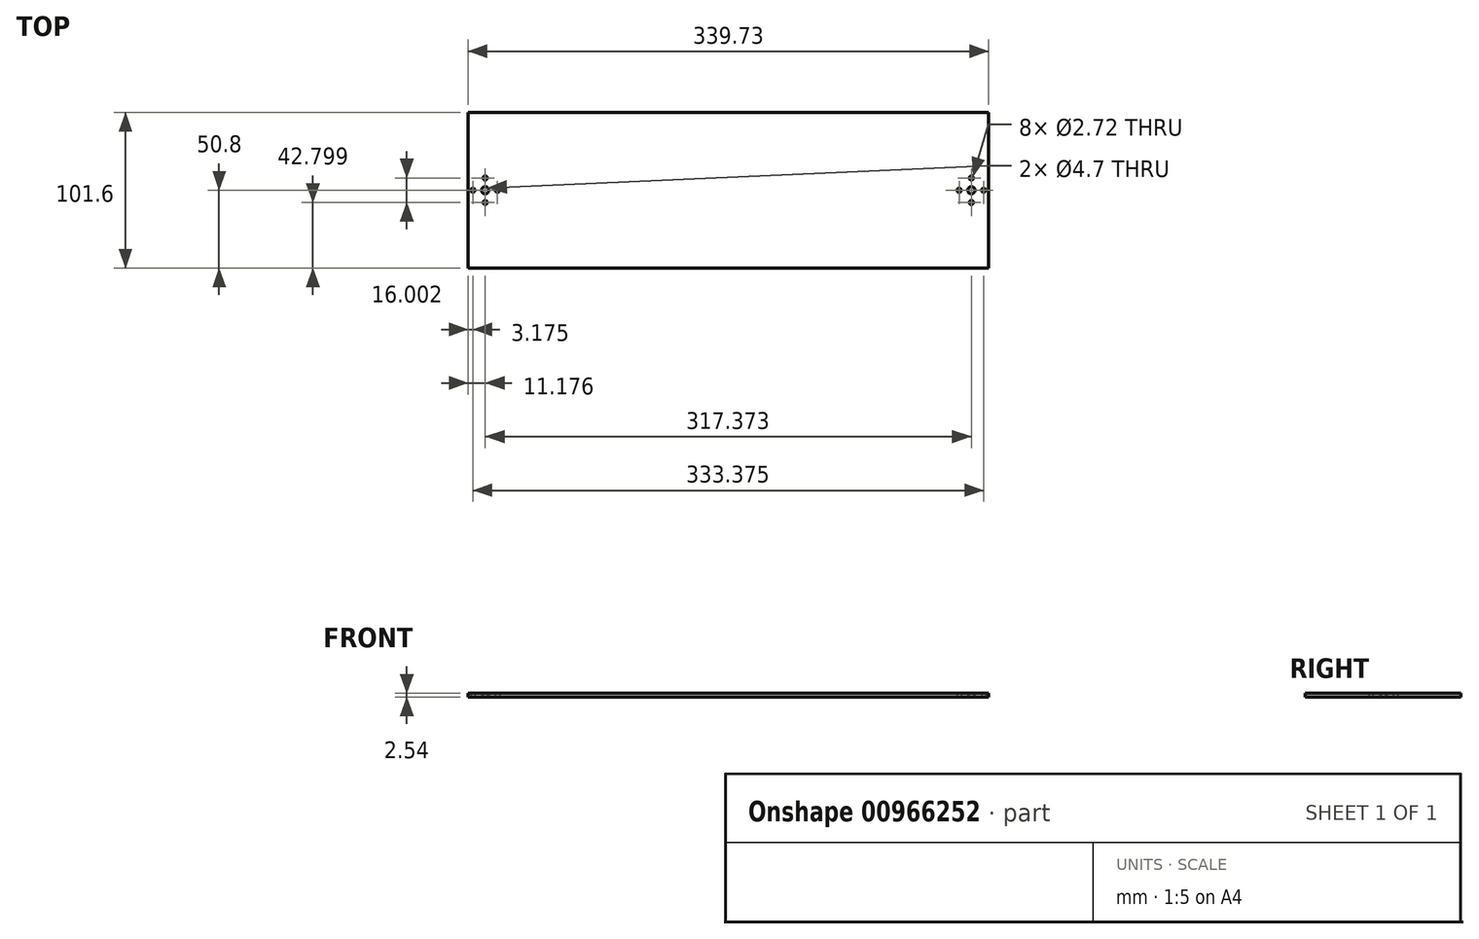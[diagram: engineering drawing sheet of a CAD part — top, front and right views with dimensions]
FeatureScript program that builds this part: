
annotation { "Feature Type Name" : "Feature", "Feature Type Description" : "" }
export const myFeature = defineFeature(function(context is Context, id is Id, definition is map)
    precondition{}
    {
        {
            var Q0;
            Q0=qCreatedBy(makeId("Top.planeOp"),FACE);
            var sketch = newSketch(context, id + "F0", { "sketchPlane" : qUnion([Q0])});
            skLineSegment(sketch, "E0.bottom", {"start": v(0, 0) * mm, "end": v(339.73, 0) * mm});
            skLineSegment(sketch, "E0.top", {"start": v(0, -101.6) * mm, "end": v(339.73, -101.6) * mm});
            skLineSegment(sketch, "E0.left", {"start": v(0, 0) * mm, "end": v(0, -101.6) * mm});
            skLineSegment(sketch, "E0.right", {"start": v(339.73, 0) * mm, "end": v(339.73, -101.6) * mm});
            skCircle(sketch, "E1", {"center": v(3.17, -50.8) * mm, "radius": 1.36 * mm});
            skPoint(sketch, "E1.centerSnap0", {"position": v(0, -50.8) * mm});
            skCircle(sketch, "E2", {"center": v(19.18, -50.8) * mm, "radius": 1.36 * mm});
            skCircle(sketch, "E3", {"center": v(11.18, -42.8) * mm, "radius": 1.36 * mm});
            skCircle(sketch, "E4", {"center": v(11.18, -58.8) * mm, "radius": 1.36 * mm});
            skCircle(sketch, "E5", {"center": v(11.18, -50.8) * mm, "radius": 2.35 * mm});
            skLineSegment(sketch, "E6", {"start": v(169.86, -101.6) * mm, "end": v(169.86, 0) * mm});
            skPoint(sketch, "E7.MirrorP", {"position": v(339.73, -50.8) * mm});
            skCircle(sketch, "E8.MirrorC", {"center": v(336.55, -50.8) * mm, "radius": 1.36 * mm});
            skCircle(sketch, "E9.MirrorC", {"center": v(320.55, -50.8) * mm, "radius": 1.36 * mm});
            skCircle(sketch, "E10.MirrorC", {"center": v(328.55, -50.8) * mm, "radius": 2.35 * mm});
            skCircle(sketch, "E11.MirrorC", {"center": v(328.55, -58.8) * mm, "radius": 1.36 * mm});
            skCircle(sketch, "E12.MirrorC", {"center": v(328.55, -42.8) * mm, "radius": 1.36 * mm});
            skSolve(sketch);
        }
        {
            var Q0;
            {var subQ0=sQuery(id+"F0.wireOp",EDGE,"E0.left");Q0=makeQuery(id+"F0.imprint","IMPRINT",FACE,{"disambiguationData":[TD([[makeQuery(id+"F0.imprint","IMPRINT",EDGE,{"derivedFrom":subQ0}),1.0]])]});}
            var Q1;
            {var subQ1=sQuery(id+"F0.wireOp",EDGE,"E0.right");Q1=makeQuery(id+"F0.imprint","IMPRINT",FACE,{"disambiguationData":[TD([[makeQuery(id+"F0.imprint","IMPRINT",EDGE,{"derivedFrom":subQ1}),-1.0]])]});}
            extrude(context, id + "F1", {"entities" : qUnion([Q0, Q1]), "depth" : 2.54 * mm});
        }
    });
